# Revit family: Plumbing Fixture-Grease_Interseptor_Mifab_MI-SAND
name_source: partatom
category: Plumbing Fixtures
revit_build: Autodesk Revit Structure 2013 (Build: 20120221_2030(x64)
units: mm (PartAtom-declared; Revit-internal decimal feet)

## types (7) — shared parameters
Assembly Code = D2090300
B = 36 "
C = 22 "
D = 38 "
Description = Sand and Grit Interceptor
E = 60 "
Interceptor Material = Acid Resistant Epoxy Coated Green
Manufacturer = MIFAB
URL = www.mifab.com
zero-valued in all types: Default Elevation, WFU

## per-type parameters (varying)
| type | A | F | Standard Inlet And Outlet Radii | Water Capacity |
| MI-SAND-1 | 60 " | 4 " | 2 " | 323 Gallons |
| MI-SAND-2 | 72 " | 4 " | 2 " | 405 Gallons |
| MI-SAND-3 | 96 " | 6 " | 3 " | 540Gallons |
| MI-SAND-4 | 108 " | 6 " | 3 " | 608 Gallons |
| MI-SAND-5 | 120 " | 6 " | 3 " | 700 Gallons |
| MI-SAND-6 | 144 " | 8 " | 4 " | 810 Gallons |
| MI-SAND-7 | 180 " | 8 " | 4 " | 1013 Gallons |

note: column(s) folded — value = type name in every type: Model

## geometry (parser evidence)
native form markers: Blend x4, Sweep x1
no freeform markers — native parametric forms only
